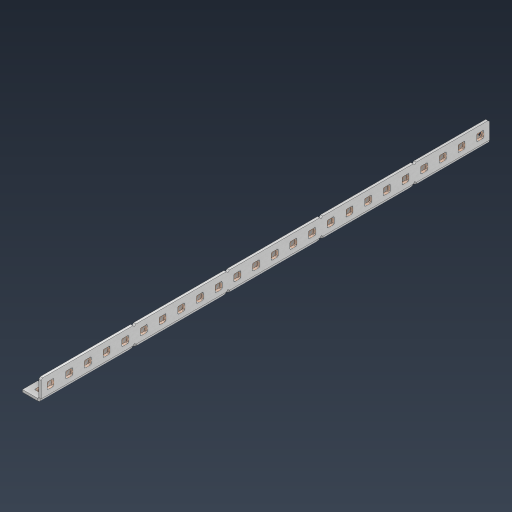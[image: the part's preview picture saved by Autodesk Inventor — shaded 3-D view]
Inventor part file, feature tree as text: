
AUTODESK INVENTOR PART (.ipt)
format: ipt  version: 2024.3 (Build 283343000, 343)  size: 967,168 bytes
history: native  units: in
note: dims shown in document units (in); Inventor stores cm internally (conversion verified against a paired STEP export)
features: other x79, extrude x70, sheet_metal_op x11, pattern_linear x2, mirror x1, chamfer x1, sketch x1
ambient origin geometry x8: Origin, YZ Plane, XZ Plane, XY Plane, X Axis, Y Axis, Z Axis, Center Point
bodies: Solid1 (feature_tree), Body (feature_tree)
feature tree (165):
  sheet_metal_op  "Flanges"
  other  "Flange Pattern Plane"
  other  "Flange Pattern Sketch"
  sheet_metal_op  "Flange Pattern"
  sheet_metal_op  "Body Pattern"
  pattern_linear  "Center Pattern"  Spacing1=12.0in  [1 undecoded]
  other  "Arc Length"
  mirror  "Notch Mirror"
  pattern_linear  "Notch Pattern"  Spacing1=0.0625in  [1 undecoded]
  chamfer  "End Chamfer"
  extrude  "Half Cut"  Depth=0.0625in
  other  "Plate1"
  sketch  "Sketch2"  dims[d0=1.0in d1=12.0in d2=0.0625in d3=0.0625in d4=0.0312in d5=0.125in d6=0.0625in d7=0.5in d8=90.0deg d9=0.0312in d10=0.25in d11=0.0625in d12=0.0625in d16=0.182in d17=0.02in d18=0.0625in d19=0.0in d20=0.25in d21=0.25in d38=9.4488in d40=0.5in d41=0.3937in d43=1.0in d46=0.172in d47=1.0in d48=0.0in d49=0.182in d50=0.02in d51=0.25in d52=0.25in d53=0.0625in d54=0.0in d55=0.172in d56=1.0in d57=0.0in d58=0.25in d60=9.4488in d62=0.5in d63=0.3937in d65=0.5in d85=0.1473in d86=0.1782in d88=0.04in d89=0.0625in d90=0.0in d91=0.04in d92=0.0491in d95=2.5in d96=0.04in d97=0.25in d98=45.0deg d99=0.25in d100=0.5in d101=0.0in d102=2.497in d106=0.182in d107=0.02in d108=0.5in d109=0.5in d110=0.0625in d111=0.0in d112=0.172in d113=0.5in d114=0.0in d117=0.5in d118=0.5in d119=0.5in]
  other  "Plate2"
  sheet_metal_op  "Bend1"
  sheet_metal_op  "Corner1"
  other  "Srf1"
  other  "Srf2"
  other  "Srf91"
  sheet_metal_op  "Body Pattern Sketch"
  other  "Srf92"
  other  "Srf786"
  other  "Srf823"
  other  "Srf824"
  other  "Srf825"
  other  "Srf826"
  other  "Srf827"
  other  "Srf828"
  other  "Srf829"
  other  "Srf856"
  other  "Srf857"
  other  "Srf858"
  other  "Srf859"
  other  "Srf860"
  other  "Srf861"
  other  "Srf862"
  other  "Srf889"
  other  "Srf890"
  other  "Srf891"
  other  "Srf892"
  other  "Srf893"
  other  "Srf894"
  other  "Srf895"
  other  "Srf896"
  other  "Srf922"
  other  "Srf923"
  other  "Srf924"
  other  "Srf925"
  other  "Srf926"
  other  "Srf959"
  other  "Srf960"
  other  "Srf961"
  other  "Srf962"
  other  "Srf963"
  other  "Srf996"
  other  "Srf997"
  other  "Srf998"
  other  "Srf999"
  other  "Srf1000"
  other  "Srf1143"
  other  "Srf1144"
  other  "Srf1145"
  other  "Srf1146"
  other  "Srf1147"
  other  "Srf1148"
  other  "Srf1149"
  other  "Srf1150"
  other  "Srf1151"
  other  "Srf1152"
  other  "Srf1199"
  other  "Srf1200"
  other  "Srf1201"
  other  "Srf1202"
  other  "Srf1203"
  other  "Srf1204"
  other  "Srf1205"
  other  "Srf1206"
  other  "Srf1207"
  other  "Srf1208"
  other  "Srf1255"
  other  "Srf1256"
  other  "Srf1257"
  other  "Srf1258"
  other  "Srf1259"
  other  "Srf1260"
  other  "Srf1261"
  other  "Srf1262"
  other  "Srf1263"
  other  "Srf1264"
  sheet_metal_op  "Flange Stamp"
  sheet_metal_op  "Flange Circle"
  sheet_metal_op  "Body Stamp"
  sheet_metal_op  "Body Circle"
  other  "Center Stamp"
  other  "Center Circle"
  sheet_metal_op  "Notch"
  extrude  "ExtrusionSrf2"  Depth=0.0312in
  extrude  "ExtrusionSrf92"  Depth=0.5in
  extrude  "ExtrusionSrf823"  Depth=0.0625in
  extrude  "ExtrusionSrf824"  Depth=0.5in TaperAngle=90.0deg
  extrude  "ExtrusionSrf825"  Depth=0.25in
  extrude  "ExtrusionSrf826"  Depth=0.0625in
  extrude  "ExtrusionSrf827"  Depth=0.0625in
  extrude  "ExtrusionSrf828"  Depth=0.182in
  extrude  "ExtrusionSrf829"  Depth=0.02in
  extrude  "ExtrusionSrf856"  Depth=0.0625in
  extrude  "ExtrusionSrf857"  TaperAngle=0.0deg  [1 undecoded]
  extrude  "ExtrusionSrf858"  Depth=0.25in
  extrude  "ExtrusionSrf859"  Depth=0.25in
  extrude  "ExtrusionSrf860"  Depth=0.5in
  extrude  "ExtrusionSrf861"  Depth=0.5in
  extrude  "ExtrusionSrf862"  Depth=1.0in TaperAngle=0.0deg
  extrude  "ExtrusionSrf889"  Depth=0.182in
  extrude  "ExtrusionSrf890"  Depth=0.02in
  extrude  "ExtrusionSrf891"  Depth=0.25in
  extrude  "ExtrusionSrf892"  Depth=0.25in
  extrude  "ExtrusionSrf893"  Depth=0.0625in
  extrude  "ExtrusionSrf894"  TaperAngle=0.0deg  [1 undecoded]
  extrude  "ExtrusionSrf895"  Depth=0.5in
  extrude  "ExtrusionSrf896"  Depth=1.0in TaperAngle=0.0deg
  extrude  "ExtrusionSrf922"  Depth=0.25in
  extrude  "ExtrusionSrf923"  Depth=0.5in
  extrude  "ExtrusionSrf924"  Depth=0.5in
  extrude  "ExtrusionSrf925"  Depth=0.5in
  extrude  "ExtrusionSrf926"  Depth=0.5in
  extrude  "ExtrusionSrf959"  Depth=0.5in
  extrude  "ExtrusionSrf960"  Depth=0.0625in
  extrude  "ExtrusionSrf961"  TaperAngle=0.0deg  [1 undecoded]
  extrude  "ExtrusionSrf962"  Depth=0.5in
  extrude  "ExtrusionSrf963"  Depth=0.5in
  extrude  "ExtrusionSrf996"  Depth=2.5in
  extrude  "ExtrusionSrf997"  Depth=0.25in TaperAngle=45.0deg
  extrude  "ExtrusionSrf998"  Depth=0.25in
  extrude  "ExtrusionSrf999"  Depth=0.5in TaperAngle=0.0deg
  extrude  "ExtrusionSrf1000"  Depth=0.5in
  extrude  "ExtrusionSrf1143"  Depth=0.182in
  extrude  "ExtrusionSrf1144"  Depth=0.02in
  extrude  "ExtrusionSrf1145"  Depth=0.5in
  extrude  "ExtrusionSrf1146"  Depth=0.5in
  extrude  "ExtrusionSrf1147"  Depth=0.0625in
  extrude  "ExtrusionSrf1148"  TaperAngle=0.0deg  [1 undecoded]
  extrude  "ExtrusionSrf1149"  Depth=0.5in
  extrude  "ExtrusionSrf1150"  Depth=0.5in TaperAngle=0.0deg
  extrude  "ExtrusionSrf1151"  Depth=0.5in
  extrude  "ExtrusionSrf1152"  Depth=0.5in
  extrude  "ExtrusionSrf1199"  Depth=0.5in
  extrude  "ExtrusionSrf1200"  [1 undecoded]
  extrude  "ExtrusionSrf1201"  [1 undecoded]
  extrude  "ExtrusionSrf1202"  [1 undecoded]
  extrude  "ExtrusionSrf1203"  [1 undecoded]
  extrude  "ExtrusionSrf1204"  [1 undecoded]
  extrude  "ExtrusionSrf1205"  [1 undecoded]
  extrude  "ExtrusionSrf1206"  [1 undecoded]
  extrude  "ExtrusionSrf1207"  [1 undecoded]
  extrude  "ExtrusionSrf1208"  [1 undecoded]
  extrude  "ExtrusionSrf1255"  [1 undecoded]
  extrude  "ExtrusionSrf1256"  [1 undecoded]
  extrude  "ExtrusionSrf1257"  [1 undecoded]
  extrude  "ExtrusionSrf1258"  [1 undecoded]
  extrude  "ExtrusionSrf1259"  [1 undecoded]
  extrude  "ExtrusionSrf1260"  [1 undecoded]
  extrude  "ExtrusionSrf1261"  [1 undecoded]
  extrude  "ExtrusionSrf1262"  [1 undecoded]
  extrude  "ExtrusionSrf1263"  [1 undecoded]
  extrude  "ExtrusionSrf1264"  [1 undecoded]
note: 25 required parameter values undecoded (feature->parameter linkage not recoverable at this tier; creation-order binding heuristic only, values carry confidence <= 0.55)
